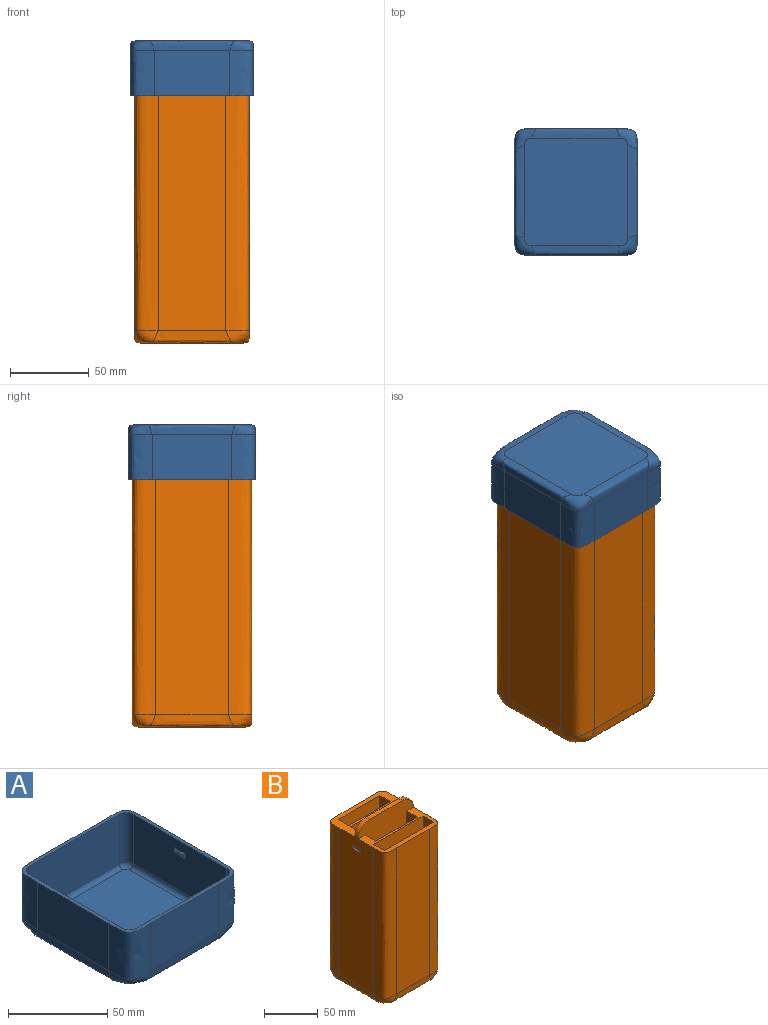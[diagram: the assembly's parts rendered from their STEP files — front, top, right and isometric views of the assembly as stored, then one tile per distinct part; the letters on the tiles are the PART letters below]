
ASSEMBLY  parts=2 mates=1
PART A: 45 faces, bbox 80.3x82.8x40.8 mm
  f0: plane 66.5x30.5mm, normal (1,0,0), area 2009.5mm2, adj f2,f11,f12,f33,f41,f42,f43,f44
  f1: plane 66.5x30.5mm, normal (-1,0,0), area 2009.5mm2, adj f2,f13,f14,f28,f36,f37,f38,f39
  f2: plane 82.76x80.26mm, normal (0,0,1), area 568.6mm2, adj f0,f1,f3,f4,f5,f6,f8,f9
  f3: plane 48x29mm, normal (0,-1,0), area 1392mm2, adj f2,f17,f18,f20
  f4: plane 50.5x29mm, normal (1,0,0), area 1464.5mm2, adj f2,f16,f18,f22
  f5: plane 48x29mm, normal (0,1,0), area 1392mm2, adj f2,f15,f16,f21
  f6: plane 50.5x29mm, normal (-1,0,0), area 1464.5mm2, adj f2,f15,f17,f19
  f7: plane 68.98x66.48mm, normal (0,0,-1), area 4500.9mm2, adj f19,f20,f21,f22,f23,f24,f25,f26
  f8: plane 64x30.5mm, normal (0,1,0), area 1952mm2, adj f2,f12,f14,f29
  f9: plane 64x30.5mm, normal (0,-1,0), area 1952mm2, adj f2,f11,f13,f32
  f10: plane 71.5x69mm, normal (0,0,1), area 4928.1mm2, adj f27,f28,f29,f30,f31,f32,f33,f34
  f11: cylinder r=5mm len=30.5mm, axis (0,0,-1), area 239.5mm2, adj f0,f2,f9,f34
  f12: cylinder r=5mm len=30.5mm, axis (0,0,1), area 239.5mm2, adj f0,f2,f8,f31
  f13: cylinder r=5mm len=30.5mm, axis (0,0,1), area 239.5mm2, adj f1,f2,f9,f30
  f14: cylinder r=5mm len=30.5mm, axis (0,0,-1), area 239.5mm2, adj f1,f2,f8,f27
  f15: bspline ~38.5x15mm, area 784.3mm2, adj f2,f5,f6,f24
  f16: bspline ~38.5x15mm, area 784.3mm2, adj f2,f4,f5,f26
  f17: bspline ~38.5x15mm, area 784.3mm2, adj f2,f3,f6,f23
  f18: bspline ~38.5x15mm, area 784.3mm2, adj f2,f3,f4,f25
  f19: bspline ~68.5x6mm, area 589.4mm2, adj f6,f7,f23,f24
  f20: bspline ~66x6mm, area 562.3mm2, adj f3,f7,f23,f25
  f21: bspline ~60.99x6mm, area 562.3mm2, adj f5,f7,f24,f26
  f22: bspline ~63.49x6mm, area 589.4mm2, adj f4,f7,f25,f26
  f23: bspline ~15.52x15.37mm, area 193.7mm2, adj f7,f17,f19,f20
  f24: bspline ~15.52x15.37mm, area 193.7mm2, adj f7,f15,f19,f21
  f25: bspline ~15.52x15.37mm, area 193.7mm2, adj f7,f18,f20,f22
  f26: bspline ~15.52x15.37mm, area 193.7mm2, adj f7,f16,f21,f22
  f27: torus R=2.5mm, axis (0,0,1), area 25.2mm2, adj f10,f14,f28,f29
  f28: cylinder r=2.5mm len=66.5mm, axis (0,-1,0), area 261.1mm2, adj f1,f10,f27,f30
  f29: cylinder r=2.5mm len=64mm, axis (-1,0,0), area 251.3mm2, adj f8,f10,f27,f31
  f30: torus R=2.5mm, axis (0,0,1), area 25.2mm2, adj f10,f13,f28,f32
  f31: torus R=2.5mm, axis (0,0,1), area 25.2mm2, adj f10,f12,f29,f33
  f32: cylinder r=2.5mm len=64mm, axis (1,0,0), area 251.3mm2, adj f9,f10,f30,f34
  f33: cylinder r=2.5mm len=66.5mm, axis (0,1,0), area 261.1mm2, adj f0,f10,f31,f34
  f34: torus R=2.5mm, axis (0,0,1), area 25.2mm2, adj f10,f11,f32,f33
  f35: plane 5.5x0.5mm, normal (-1,0,0), area 2.8mm2, adj f36,f37,f38,f39
  f36: cylinder r=1mm len=7.5mm, axis (0,-1,0), area 10.2mm2, adj f1,f35,f37,f38
  f37: cylinder r=1mm len=2.5mm, axis (0,0,-1), area 2.4mm2, adj f1,f35,f36,f39
  f38: cylinder r=1mm len=2.5mm, axis (0,0,1), area 2.4mm2, adj f1,f35,f36,f39
  f39: cylinder r=1mm len=7.5mm, axis (0,1,0), area 10.2mm2, adj f1,f35,f37,f38
  f40: plane 5.5x0.5mm, normal (1,0,0), area 2.8mm2, adj f41,f42,f43,f44
  f41: cylinder r=1mm len=7.5mm, axis (0,-1,0), area 10.2mm2, adj f0,f40,f42,f43
  f42: cylinder r=1mm len=2.5mm, axis (0,0,1), area 2.4mm2, adj f0,f40,f41,f44
  f43: cylinder r=1mm len=2.5mm, axis (0,0,-1), area 2.4mm2, adj f0,f40,f41,f44
  f44: cylinder r=1mm len=7.5mm, axis (0,1,0), area 10.2mm2, adj f0,f40,f42,f43
PART B: 60 faces, bbox 75.5x78.5x211.5 mm
  f0: plane 167.21x46mm, normal (-1,0,0), area 7641.5mm2, adj f6,f8,f10,f23,f56,f57,f58,f59
  f1: plane 167.21x46mm, normal (1,0,0), area 7641.5mm2, adj f7,f9,f13,f22,f51,f52,f53,f54
  f2: plane 167.21x43mm, normal (0,1,0), area 7189.9mm2, adj f6,f7,f12,f21
  f3: plane 167.21x43mm, normal (0,-1,0), area 7189.9mm2, adj f8,f9,f11,f19
  f4: plane 43.4x5mm, normal (0,0,1), area 217mm2, adj f18,f20,f22,f23
  f5: plane 60x57mm, normal (0,0,-1), area 3420mm2, adj f10,f11,f12,f13
  f6: bspline ~209x15mm, area 4521.8mm2, adj f0,f2,f15,f21
  f7: bspline ~209x15mm, area 4521.8mm2, adj f1,f2,f17,f21
  f8: bspline ~209x15mm, area 4521.8mm2, adj f0,f3,f14,f19
  f9: bspline ~209x15mm, area 4521.8mm2, adj f1,f3,f16,f19
  f10: bspline ~60x8mm, area 764.4mm2, adj f0,f5,f14,f15
  f11: bspline ~57x8mm, area 721.2mm2, adj f3,f5,f14,f16
  f12: bspline ~57x8mm, area 721.2mm2, adj f2,f5,f15,f17
  f13: bspline ~60x8mm, area 764.4mm2, adj f1,f5,f16,f17
  f14: bspline ~17x16.55mm, area 109.4mm2, adj f8,f10,f11
  f15: bspline ~17x16.55mm, area 109.4mm2, adj f6,f10,f12
  f16: bspline ~17x16.55mm, area 109.4mm2, adj f9,f11,f13
  f17: bspline ~17x16.55mm, area 109.4mm2, adj f7,f12,f13
  f18: plane 142x73mm, normal (0,-1,0), area 5942.3mm2, adj f4,f19,f22,f23,f29,f30,f41,f42
  f19: plane 75.48x37.97mm, normal (0,0,1), area 889.2mm2, adj f3,f8,f9,f18,f22,f23,f24,f25
  f20: plane 142x73mm, normal (0,1,0), area 5942.3mm2, adj f4,f21,f22,f23,f32,f33,f44,f45
  f21: plane 75.48x37.97mm, normal (0,0,1), area 1029.2mm2, adj f2,f6,f7,f20,f22,f23,f31,f32
  f22: cylinder r=14.8mm len=46mm, axis (0,-1,0), area 116.5mm2, adj f1,f4,f18,f19,f20,f21
  f23: cylinder r=14.8mm len=46mm, axis (0,1,0), area 116.5mm2, adj f0,f4,f18,f19,f20,f21
  f24: plane 168.71x65mm, normal (0,1,0), area 7737.2mm2, adj f19,f25,f27,f38,f39,f40
  f25: plane 25.21x14mm, normal (1,0,0), area 352.9mm2, adj f19,f24,f26,f39
  f26: plane 168.71x65mm, normal (0,-1,0), area 7737.2mm2, adj f19,f25,f27,f38,f39,f40
  f27: plane 25.21x14mm, normal (-1,0,0), area 352.9mm2, adj f19,f24,f26,f40
  f28: plane 127.21x55mm, normal (0,1,0), area 4956.4mm2, adj f19,f29,f30,f41,f42,f43
  f29: plane 25.21x14mm, normal (-1,0,0), area 352.9mm2, adj f18,f19,f28,f43
  f30: plane 25.21x14mm, normal (1,0,0), area 352.9mm2, adj f18,f19,f28,f42
  f31: plane 127.21x55mm, normal (0,-1,0), area 4956.4mm2, adj f21,f32,f33,f44,f45,f46
  f32: plane 25.21x14mm, normal (-1,0,0), area 352.9mm2, adj f20,f21,f31,f46
  f33: plane 25.21x14mm, normal (1,0,0), area 352.9mm2, adj f20,f21,f31,f45
  f34: plane 113.21x55mm, normal (0,1,0), area 4334.4mm2, adj f21,f35,f37,f47,f48,f49
  f35: plane 25.21x14mm, normal (1,0,0), area 352.9mm2, adj f21,f34,f36,f48
  f36: plane 113.21x55mm, normal (0,-1,0), area 4334.4mm2, adj f21,f35,f37,f47,f48,f49
  f37: plane 25.21x14mm, normal (-1,0,0), area 352.9mm2, adj f21,f34,f36,f49
  f38: plane 20x14mm, normal (0,0,1), area 280mm2, adj f24,f26,f39,f40
  f39: plane 143.5x22.5mm, normal (0.99,0,0.15), area 2033.5mm2, adj f24,f25,f26,f38
  f40: plane 143.5x22.5mm, normal (-0.99,0,0.15), area 2033.5mm2, adj f24,f26,f27,f38
  f41: plane 15x14mm, normal (0,0,1), area 210mm2, adj f18,f28,f42,f43
  f42: plane 102x20mm, normal (0.98,0,0.19), area 1455.2mm2, adj f18,f28,f30,f41
  f43: plane 102x20mm, normal (-0.98,0,0.19), area 1455.2mm2, adj f18,f28,f29,f41
  f44: plane 15x14mm, normal (0,0,1), area 210mm2, adj f20,f31,f45,f46
  f45: plane 102x20mm, normal (0.98,0,0.19), area 1455.2mm2, adj f20,f31,f33,f44
  f46: plane 102x20mm, normal (-0.98,0,0.19), area 1455.2mm2, adj f20,f31,f32,f44
  f47: plane 14x12mm, normal (0,0,1), area 168mm2, adj f34,f36,f48,f49
  f48: plane 88x21.5mm, normal (0.97,0,0.24), area 1268.2mm2, adj f34,f35,f36,f47
  f49: plane 88x21.5mm, normal (-0.97,0,0.24), area 1268.2mm2, adj f34,f36,f37,f47
  f50: plane 8x3mm, normal (1,0,0), area 24mm2, adj f51,f52,f53,f54
  f51: cylinder r=1mm len=10mm, axis (0,1,0), area 14.1mm2, adj f1,f50,f52,f53
  f52: cylinder r=1mm len=5mm, axis (0,0,1), area 6.3mm2, adj f1,f50,f51,f54
  f53: cylinder r=1mm len=5mm, axis (0,0,-1), area 6.3mm2, adj f1,f50,f51,f54
  f54: cylinder r=1mm len=10mm, axis (0,-1,0), area 14.1mm2, adj f1,f50,f52,f53
  f55: plane 8x3mm, normal (-1,0,0), area 24mm2, adj f56,f57,f58,f59
  f56: cylinder r=1mm len=5mm, axis (0,0,1), area 6.3mm2, adj f0,f55,f57,f58
  f57: cylinder r=1mm len=10mm, axis (0,1,0), area 14.1mm2, adj f0,f55,f56,f59
  f58: cylinder r=1mm len=10mm, axis (0,-1,0), area 14.1mm2, adj f0,f55,f56,f59
  f59: cylinder r=1mm len=5mm, axis (0,0,-1), area 6.3mm2, adj f0,f55,f57,f58
PLACE A rot(axis=(1,0,0),180deg) t=(-85.98,-19.09,23.47)mm
PLACE B t=(-85.98,-19.09,-168.53)mm
MATE fastened A.f10 <-> B.f4  axis (0,0,-1) through (-85.98,-19.09,21.47)mm
